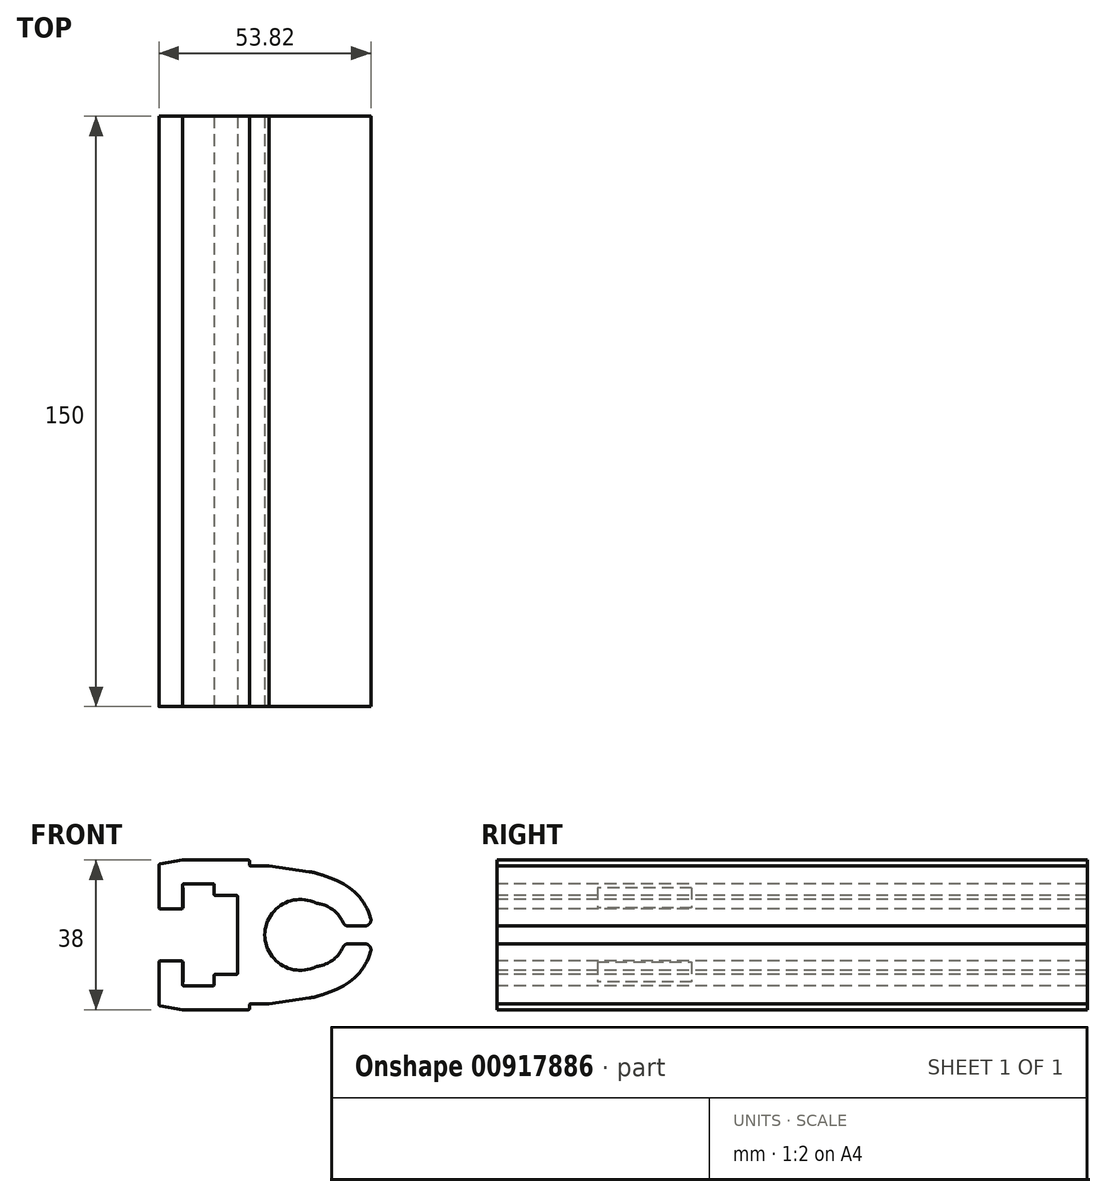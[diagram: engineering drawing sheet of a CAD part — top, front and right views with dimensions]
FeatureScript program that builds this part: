
annotation { "Feature Type Name" : "Feature", "Feature Type Description" : "" }
export const myFeature = defineFeature(function(context is Context, id is Id, definition is map)
    precondition{}
    {
        {
            var Q0;
            Q0=qCreatedBy(makeId("Front.planeOp"),FACE);
            var sketch = newSketch(context, id + "F0", { "sketchPlane" : qUnion([Q0])});
            skLineSegment(sketch, "E0", {"start": v(57.08, -14.1) * mm, "end": v(54, -15.22) * mm});
            skArc(sketch, "E1", {"start": v(50.71, -16.04) * mm, "mid": v(52.37, -15.72) * mm, "end": v(54, -15.22) * mm});
            skLineSegment(sketch, "E2", {"start": v(50.71, -16.04) * mm, "end": v(40.59, -17.47) * mm});
            skLineSegment(sketch, "E3", {"start": v(40.59, -17.47) * mm, "end": v(35.89, -17.47) * mm});
            skArc(sketch, "E4", {"start": v(35.89, -17.47) * mm, "mid": v(35.67, -17.55) * mm, "end": v(35.59, -17.77) * mm});
            skLineSegment(sketch, "E5", {"start": v(35.59, -17.77) * mm, "end": v(35.59, -18.7) * mm});
            skArc(sketch, "E6", {"start": v(35.29, -19) * mm, "mid": v(35.5, -18.91) * mm, "end": v(35.59, -18.7) * mm});
            skLineSegment(sketch, "E7", {"start": v(35.29, -19) * mm, "end": v(18.59, -19) * mm});
            skLineSegment(sketch, "E8", {"start": v(18.59, -19) * mm, "end": v(12.84, -18.04) * mm});
            skArc(sketch, "E9", {"start": v(12.59, -17.75) * mm, "mid": v(12.66, -17.94) * mm, "end": v(12.84, -18.04) * mm});
            skLineSegment(sketch, "E10", {"start": v(12.59, -17.75) * mm, "end": v(12.59, -6.87) * mm});
            skArc(sketch, "E11", {"start": v(12.89, -6.58) * mm, "mid": v(12.67, -6.66) * mm, "end": v(12.59, -6.88) * mm});
            skLineSegment(sketch, "E12", {"start": v(12.89, -6.58) * mm, "end": v(18.29, -6.58) * mm});
            skArc(sketch, "E13", {"start": v(18.59, -6.88) * mm, "mid": v(18.5, -6.66) * mm, "end": v(18.29, -6.58) * mm});
            skLineSegment(sketch, "E14", {"start": v(18.59, -6.88) * mm, "end": v(18.59, -12.7) * mm});
            skArc(sketch, "E15", {"start": v(18.59, -12.7) * mm, "mid": v(18.67, -12.91) * mm, "end": v(18.89, -13) * mm});
            skLineSegment(sketch, "E16", {"start": v(18.89, -13) * mm, "end": v(26.29, -13) * mm});
            skArc(sketch, "E17", {"start": v(26.29, -13) * mm, "mid": v(26.5, -12.91) * mm, "end": v(26.59, -12.7) * mm});
            skLineSegment(sketch, "E18", {"start": v(26.59, -12.7) * mm, "end": v(26.59, -10.3) * mm});
            skArc(sketch, "E19", {"start": v(26.89, -10) * mm, "mid": v(26.67, -10.09) * mm, "end": v(26.59, -10.3) * mm});
            skLineSegment(sketch, "E20", {"start": v(26.89, -10) * mm, "end": v(32.29, -10) * mm});
            skArc(sketch, "E21", {"start": v(32.29, -10) * mm, "mid": v(32.5, -9.91) * mm, "end": v(32.59, -9.7) * mm});
            skLineSegment(sketch, "E22", {"start": v(32.59, -9.7) * mm, "end": v(32.59, 9.7) * mm});
            skArc(sketch, "E23", {"start": v(32.59, 9.7) * mm, "mid": v(32.5, 9.91) * mm, "end": v(32.29, 10) * mm});
            skLineSegment(sketch, "E24", {"start": v(32.29, 10) * mm, "end": v(26.89, 10) * mm});
            skArc(sketch, "E25", {"start": v(26.59, 10.3) * mm, "mid": v(26.67, 10.09) * mm, "end": v(26.89, 10) * mm});
            skLineSegment(sketch, "E26", {"start": v(26.59, 10.3) * mm, "end": v(26.59, 12.7) * mm});
            skArc(sketch, "E27", {"start": v(26.59, 12.7) * mm, "mid": v(26.5, 12.91) * mm, "end": v(26.29, 13) * mm});
            skLineSegment(sketch, "E28", {"start": v(26.29, 13) * mm, "end": v(18.89, 13) * mm});
            skArc(sketch, "E29", {"start": v(18.89, 13) * mm, "mid": v(18.67, 12.91) * mm, "end": v(18.59, 12.7) * mm});
            skLineSegment(sketch, "E30", {"start": v(18.59, 12.7) * mm, "end": v(18.59, 6.88) * mm});
            skArc(sketch, "E31", {"start": v(18.29, 6.58) * mm, "mid": v(18.5, 6.66) * mm, "end": v(18.59, 6.88) * mm});
            skLineSegment(sketch, "E32", {"start": v(18.29, 6.57) * mm, "end": v(12.89, 6.57) * mm});
            skArc(sketch, "E33", {"start": v(12.59, 6.88) * mm, "mid": v(12.67, 6.66) * mm, "end": v(12.89, 6.58) * mm});
            skLineSegment(sketch, "E34", {"start": v(12.59, 6.88) * mm, "end": v(12.59, 17.75) * mm});
            skArc(sketch, "E35", {"start": v(12.84, 18.04) * mm, "mid": v(12.66, 17.94) * mm, "end": v(12.59, 17.75) * mm});
            skLineSegment(sketch, "E36", {"start": v(12.84, 18.04) * mm, "end": v(18.59, 19) * mm});
            skLineSegment(sketch, "E37", {"start": v(18.59, 19) * mm, "end": v(35.29, 19) * mm});
            skArc(sketch, "E38", {"start": v(35.59, 18.7) * mm, "mid": v(35.5, 18.91) * mm, "end": v(35.29, 19) * mm});
            skLineSegment(sketch, "E39", {"start": v(35.59, 18.7) * mm, "end": v(35.59, 17.76) * mm});
            skArc(sketch, "E40", {"start": v(35.59, 17.76) * mm, "mid": v(35.67, 17.55) * mm, "end": v(35.89, 17.46) * mm});
            skLineSegment(sketch, "E41", {"start": v(35.89, 17.46) * mm, "end": v(40.59, 17.46) * mm});
            skLineSegment(sketch, "E42", {"start": v(40.59, 17.46) * mm, "end": v(50.71, 16.04) * mm});
            skArc(sketch, "E43", {"start": v(54, 15.22) * mm, "mid": v(52.37, 15.72) * mm, "end": v(50.71, 16.04) * mm});
            skLineSegment(sketch, "E44", {"start": v(54, 15.22) * mm, "end": v(57.08, 14.1) * mm});
            skArc(sketch, "E45", {"start": v(66.35, 4.2) * mm, "mid": v(62.9, 10.25) * mm, "end": v(57.08, 14.1) * mm});
            skArc(sketch, "E46", {"start": v(64.91, 2.27) * mm, "mid": v(66.11, 2.87) * mm, "end": v(66.35, 4.2) * mm});
            skLineSegment(sketch, "E47", {"start": v(64.91, 2.27) * mm, "end": v(60.67, 2.27) * mm});
            skArc(sketch, "E48", {"start": v(59.3, 3.18) * mm, "mid": v(59.85, 2.52) * mm, "end": v(60.67, 2.27) * mm});
            skArc(sketch, "E49", {"start": v(59.3, 3.18) * mm, "mid": v(56.98, 6.22) * mm, "end": v(53.52, 7.84) * mm});
            skArc(sketch, "E50", {"start": v(51.79, 8.36) * mm, "mid": v(52.64, 8.06) * mm, "end": v(53.52, 7.84) * mm});
            skArc(sketch, "E51", {"start": v(51.79, 8.36) * mm, "mid": v(39.45, 0) * mm, "end": v(51.79, -8.36) * mm});
            skArc(sketch, "E52", {"start": v(53.52, -7.84) * mm, "mid": v(52.64, -8.06) * mm, "end": v(51.79, -8.36) * mm});
            skArc(sketch, "E53", {"start": v(53.52, -7.84) * mm, "mid": v(56.98, -6.22) * mm, "end": v(59.3, -3.18) * mm});
            skArc(sketch, "E54", {"start": v(60.67, -2.28) * mm, "mid": v(59.85, -2.52) * mm, "end": v(59.3, -3.18) * mm});
            skLineSegment(sketch, "E55", {"start": v(60.67, -2.28) * mm, "end": v(64.91, -2.28) * mm});
            skArc(sketch, "E56", {"start": v(66.35, -4.2) * mm, "mid": v(66.11, -2.87) * mm, "end": v(64.91, -2.28) * mm});
            skArc(sketch, "E57", {"start": v(57.08, -14.1) * mm, "mid": v(62.9, -10.25) * mm, "end": v(66.35, -4.2) * mm});
            skSolve(sketch);
        }
        {
            var Q0;
            Q0=makeQuery(id+"F0.imprint","IMPRINT",FACE,{"disambiguationData":[TD([[makeQuery(id+"F0.imprint","IMPRINT",EDGE,{"derivedFrom":sQuery(id+"F0.wireOp",EDGE,"E0")}),-1.0]])]});
            extrude(context, id + "F1", {"entities" : qUnion([Q0]), "depth" : -150 * mm, "offsetDistance" : 25 * mm});
        }
        {
            var Q0;
            Q0=makeQuery(id+"F1.opExtrude","SWEPT_FACE",FACE,{"disambiguationData":[OSD([sQuery(id+"F0.wireOp",EDGE,"E30")])]});
            var sketch = newSketch(context, id + "F2", { "sketchPlane" : qUnion([Q0])});
            skLineSegment(sketch, "E58.bottom", {"start": v(49.5, 12) * mm, "end": v(25.5, 12) * mm});
            skLineSegment(sketch, "E58.top", {"start": v(49.5, -12) * mm, "end": v(25.5, -12) * mm});
            skLineSegment(sketch, "E58.left", {"start": v(25.5, 12) * mm, "end": v(25.5, -12) * mm});
            skLineSegment(sketch, "E58.right", {"start": v(49.5, 12) * mm, "end": v(49.5, -12) * mm});
            skLineSegment(sketch, "E59", {"start": v(25.5, -6.87) * mm, "end": v(49.5, -6.87) * mm});
            skSolve(sketch);
        }
        {
            var Q0;
            {var subQ0=sQuery(id+"F2.wireOp",EDGE,"E58.bottom");Q0=makeQuery(id+"F2.imprint","IMPRINT",FACE,{"disambiguationData":[TD([[makeQuery(id+"F2.imprint","IMPRINT",EDGE,{"derivedFrom":subQ0}),1.0]])]});}
            extrude(context, id + "F3", {"entities" : qUnion([Q0]), "operationType" : NewBodyOperationType.ADD, "depth" : 0.1 * mm, "offsetDistance" : 25 * mm});
        }
        {
            var Q0;
            {var subQ0=sQuery(id+"F2.wireOp",EDGE,"E58.top");Q0=makeQuery(id+"F2.imprint","IMPRINT",FACE,{"disambiguationData":[TD([[makeQuery(id+"F2.imprint","IMPRINT",EDGE,{"derivedFrom":subQ0}),-1.0]])]});}
            extrude(context, id + "F4", {"entities" : qUnion([Q0]), "operationType" : NewBodyOperationType.ADD, "depth" : 0.1 * mm, "offsetDistance" : 25 * mm});
        }
    });
